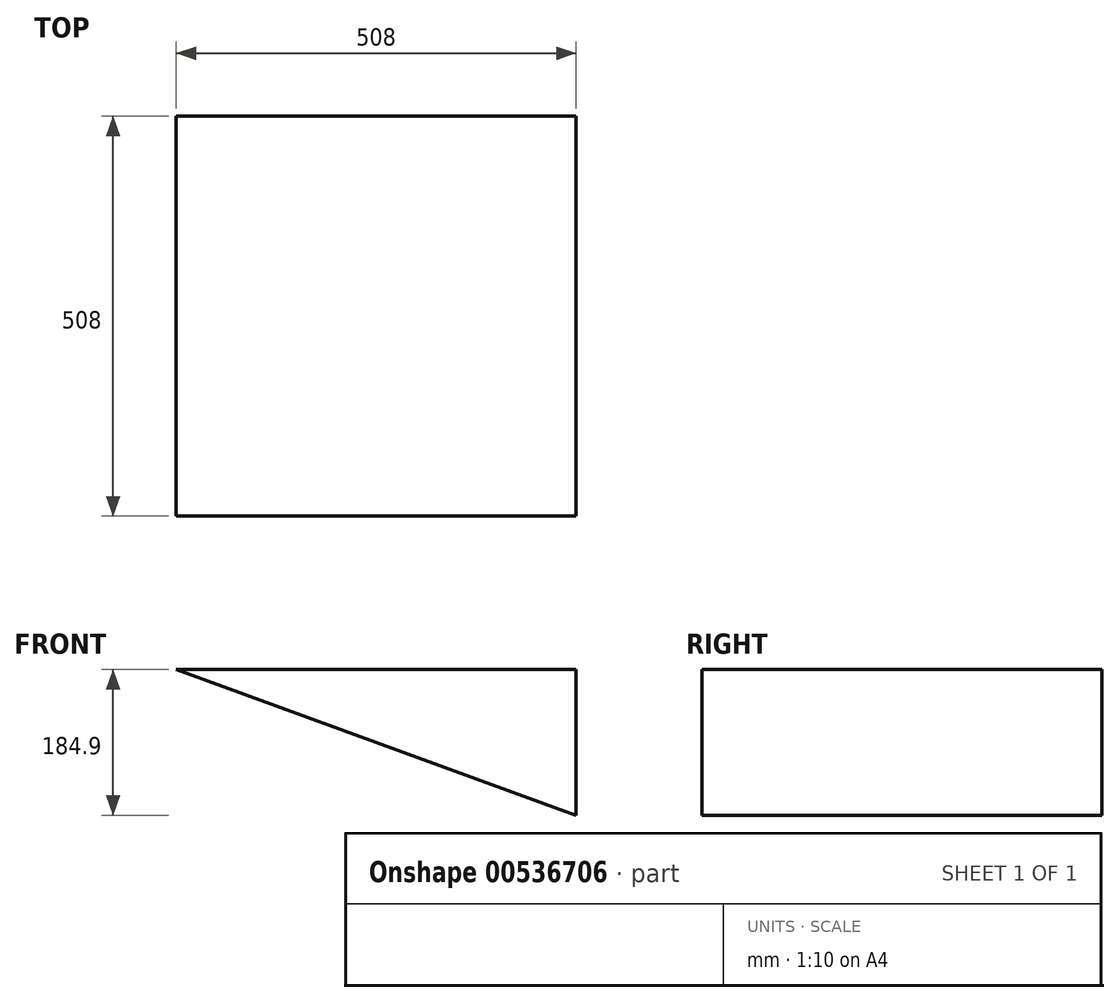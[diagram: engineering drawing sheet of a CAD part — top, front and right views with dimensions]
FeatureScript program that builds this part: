
annotation { "Feature Type Name" : "Feature", "Feature Type Description" : "" }
export const myFeature = defineFeature(function(context is Context, id is Id, definition is map)
    precondition{}
    {
        {
            var Q0;
            Q0=qCreatedBy(makeId("Front.planeOp"),FACE);
            var sketch = newSketch(context, id + "F0", { "sketchPlane" : qUnion([Q0])});
            skLineSegment(sketch, "E0", {"start": v(0, 0) * mm, "end": v(-508, 0) * mm});
            skLineSegment(sketch, "E1", {"start": v(-508, 0) * mm, "end": v(0, -184.9) * mm});
            skLineSegment(sketch, "E2", {"start": v(0, 0) * mm, "end": v(0, -184.9) * mm});
            skSolve(sketch);
        }
        {
            var Q0;
            Q0=makeQuery(id+"F0.imprint","IMPRINT",FACE,{"disambiguationData":[TD([[makeQuery(id+"F0.imprint","IMPRINT",EDGE,{"derivedFrom":sQuery(id+"F0.wireOp",EDGE,"E0")}),1.0]])]});
            extrude(context, id + "F1", {"entities" : qUnion([Q0]), "depth" : 508 * mm, "offsetDistance" : 25.4 * mm});
        }
    });
